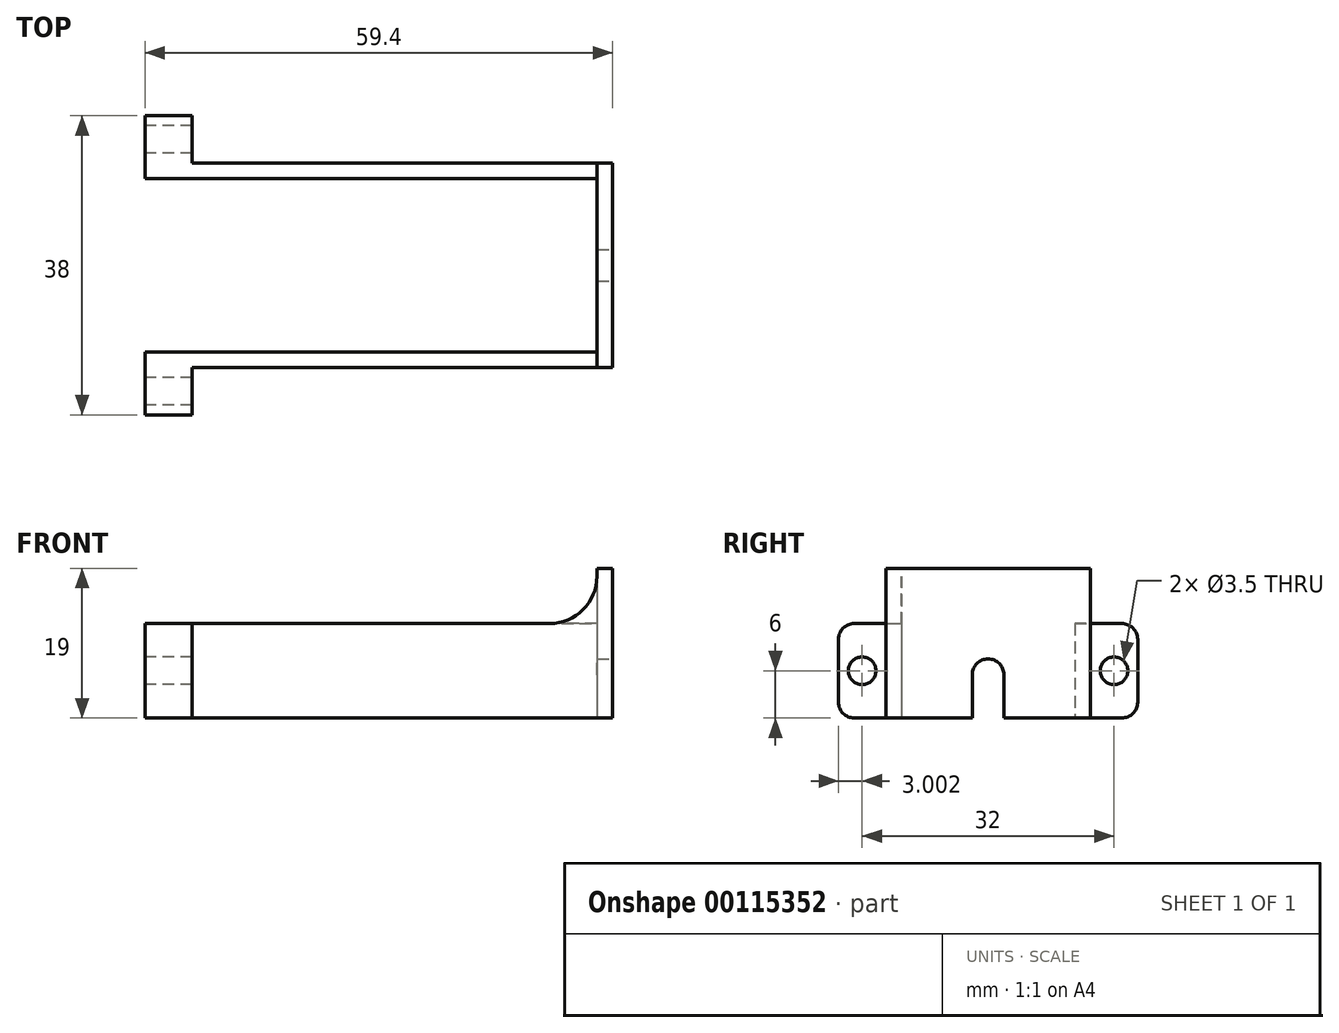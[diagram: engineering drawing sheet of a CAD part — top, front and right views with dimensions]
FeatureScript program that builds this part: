
annotation { "Feature Type Name" : "Feature", "Feature Type Description" : "" }
export const myFeature = defineFeature(function(context is Context, id is Id, definition is map)
    precondition{}
    {
        {
            var Q0;
            Q0=qCreatedBy(makeId("Top.planeOp"),FACE);
            var sketch = newSketch(context, id + "F0", { "sketchPlane" : qUnion([Q0])});
            skLineSegment(sketch, "E0", {"start": v(0, 15.1) * mm, "end": v(0, 7.1) * mm});
            skLineSegment(sketch, "E1", {"start": v(0, 7.1) * mm, "end": v(57.4, 7.1) * mm});
            skLineSegment(sketch, "E2", {"start": v(57.4, 7.1) * mm, "end": v(57.4, -3.9) * mm});
            skLineSegment(sketch, "E3", {"start": v(57.4, -3.9) * mm, "end": v(59.4, -3.9) * mm});
            skLineSegment(sketch, "E4", {"start": v(59.4, -3.9) * mm, "end": v(59.4, 9.1) * mm});
            skLineSegment(sketch, "E5", {"start": v(59.4, 9.1) * mm, "end": v(2, 9.1) * mm});
            skLineSegment(sketch, "E6", {"start": v(2, 9.1) * mm, "end": v(2, 15.1) * mm});
            skLineSegment(sketch, "E7", {"start": v(2, 15.1) * mm, "end": v(0, 15.1) * mm});
            skSolve(sketch);
        }
        {
            var Q0;
            Q0=makeQuery(id+"F0.imprint","IMPRINT",FACE,{"disambiguationData":[TD([[makeQuery(id+"F0.imprint","IMPRINT",EDGE,{"derivedFrom":sQuery(id+"F0.wireOp",EDGE,"E0")}),1.0]])]});
            extrude(context, id + "F1", {"entities" : qUnion([Q0]), "depth" : 12 * mm});
        }
        {
            var Q0;
            Q0=makeQuery(id+"F1.opExtrude","SWEPT_FACE",FACE,{"disambiguationData":[OSD([sQuery(id+"F0.wireOp",EDGE,"E0")])]});
            var sketch = newSketch(context, id + "F2", { "sketchPlane" : qUnion([Q0])});
            skLineSegment(sketch, "E8", {"start": v(-7.1, 6) * mm, "end": v(-12.1, 6) * mm, "construction": true});
            skPoint(sketch, "E8.endSnap0", {"position": v(-7.1, 6) * mm});
            skCircle(sketch, "E9", {"center": v(-12.1, 6) * mm, "radius": 1.75 * mm});
            skSolve(sketch);
        }
        {
            var Q0;
            Q0=makeQuery(id+"F1.opExtrude","SWEPT_FACE",FACE,{"disambiguationData":[OSD([sQuery(id+"F0.wireOp",EDGE,"E6")])]});
            extrude(context, id + "F3", {"entities" : qUnion([Q0]), "operationType" : NewBodyOperationType.ADD, "depth" : 4 * mm});
        }
        {
            var Q0;
            Q0=makeQuery(id+"F2.imprint","IMPRINT",FACE,{"disambiguationData":[TD([[makeQuery(id+"F2.imprint","IMPRINT",EDGE,{"derivedFrom":sQuery(id+"F2.wireOp",EDGE,"E9")}),1.0]])]});
            extrude(context, id + "F4", {"entities" : qUnion([Q0]), "operationType" : NewBodyOperationType.REMOVE, "oppositeDirection" : true, "depth" : 25 * mm});
        }
        {
            var Q0;
            {var subQ0=sQuery(id+"F0.wireOp",EDGE,"E7");var subQ1=sQuery(id+"F0.wireOp",EDGE,"E6");Q0=makeQuery(id+"F3.boolean.opBoolean","MERGE",EDGE,{"derivedFrom":[makeQuery(id+"F1.opExtrude","CAP_EDGE",EDGE,{"disambiguationData":[OSD([subQ0])],"isStart":true}),makeQuery(id+"F3.opExtrude","SWEPT_EDGE",EDGE,{"disambiguationData":[OSD([subQ1,subQ0]),TDD([makeQuery(id+"F1.opExtrude","CAP_VERTEX",VERTEX,{"disambiguationData":[OSD([subQ1,subQ0])],"isStart":true})])]})]});}
            var Q1;
            {var subQ0=sQuery(id+"F0.wireOp",EDGE,"E7");var subQ1=sQuery(id+"F0.wireOp",EDGE,"E6");Q1=makeQuery(id+"F3.boolean.opBoolean","MERGE",EDGE,{"derivedFrom":[makeQuery(id+"F1.opExtrude","CAP_EDGE",EDGE,{"disambiguationData":[OSD([subQ0])],"isStart":false}),makeQuery(id+"F3.opExtrude","SWEPT_EDGE",EDGE,{"disambiguationData":[OSD([subQ1,subQ0]),TDD([makeQuery(id+"F1.opExtrude","CAP_VERTEX",VERTEX,{"disambiguationData":[OSD([subQ1,subQ0])],"isStart":false})])]})]});}
            fillet(context, id + "F5", {"entities" : qUnion([Q0, Q1]), "radius" : 2 * mm, "tangentPropagation" : true, "allowEdgeOverflow" : false});
        }
        {
            var Q0;
            Q0=makeQuery(id+"F1.opExtrude","SWEPT_BODY",BODY,{"disambiguationData":[OSD([sQuery(id+"F0.wireOp",EDGE,"E0"),sQuery(id+"F0.wireOp",EDGE,"E1"),sQuery(id+"F0.wireOp",EDGE,"E2"),sQuery(id+"F0.wireOp",EDGE,"E3"),sQuery(id+"F0.wireOp",EDGE,"E4"),sQuery(id+"F0.wireOp",EDGE,"E5"),sQuery(id+"F0.wireOp",EDGE,"E6"),sQuery(id+"F0.wireOp",EDGE,"E7")])]});
            var Q1;
            Q1=makeQuery(id+"F1.opExtrude","SWEPT_FACE",FACE,{"disambiguationData":[OSD([sQuery(id+"F0.wireOp",EDGE,"E3")])]});
            mirror(context, id + "F6", {"operationType" : NewBodyOperationType.ADD, "entities" : qUnion([Q0]), "mirrorPlane" : qUnion([Q1])});
        }
        {
            var Q0;
            {var subQ0=makeQuery(id+"F1.opExtrude","SWEPT_FACE",FACE,{"disambiguationData":[OSD([sQuery(id+"F0.wireOp",EDGE,"E4")])]});Q0=makeQuery(id+"F6.boolean.opBoolean","MERGE",FACE,{"derivedFrom":[subQ0,makeQuery(id+"F6.opPattern","COPY",FACE,{"derivedFrom":subQ0,"instanceName":"1"})]});}
            var sketch = newSketch(context, id + "F7", { "sketchPlane" : qUnion([Q0])});
            skLineSegment(sketch, "E10", {"start": v(-3.9, 0) * mm, "end": v(-3.9, 7.5) * mm, "construction": true});
            skLineSegment(sketch, "E11", {"start": v(-3.9, 7.5) * mm, "end": v(-5.9, 7.5) * mm});
            skLineSegment(sketch, "E12", {"start": v(-5.9, 7.5) * mm, "end": v(-5.9, 0) * mm});
            skLineSegment(sketch, "E13", {"start": v(-3.9, 7.5) * mm, "end": v(-1.9, 7.5) * mm});
            skLineSegment(sketch, "E14", {"start": v(-1.9, 7.5) * mm, "end": v(-1.9, 0) * mm});
            skSolve(sketch);
        }
        {
            var Q0;
            Q0=makeQuery(id+"F7.imprint","IMPRINT",FACE,{"disambiguationData":[TD([[makeQuery(id+"F7.imprint","IMPRINT",EDGE,{"derivedFrom":sQuery(id+"F7.wireOp",EDGE,"E11")}),1.0]])]});
            extrude(context, id + "F8", {"entities" : qUnion([Q0]), "operationType" : NewBodyOperationType.REMOVE, "oppositeDirection" : true, "depth" : 25 * mm});
        }
        {
            var Q0;
            {var subQ0=sQuery(id+"F0.wireOp",EDGE,"E6");var subQ1=makeQuery(id+"F3.boolean.opBoolean","MERGE",FACE,{"derivedFrom":[makeQuery(id+"F1.opExtrude","CAP_FACE",FACE,{"disambiguationData":[OSD([sQuery(id+"F0.wireOp",EDGE,"E0"),sQuery(id+"F0.wireOp",EDGE,"E1"),sQuery(id+"F0.wireOp",EDGE,"E2"),sQuery(id+"F0.wireOp",EDGE,"E3"),sQuery(id+"F0.wireOp",EDGE,"E4"),sQuery(id+"F0.wireOp",EDGE,"E5"),subQ0,sQuery(id+"F0.wireOp",EDGE,"E7")])],"isStart":false}),makeQuery(id+"F3.opExtrude","SWEPT_FACE",FACE,{"disambiguationData":[OSD([subQ0]),TDD([makeQuery(id+"F1.opExtrude","CAP_EDGE",EDGE,{"disambiguationData":[OSD([subQ0])],"isStart":false})])]})]});Q0=makeQuery(id+"F6.boolean.opBoolean","MERGE",FACE,{"derivedFrom":[subQ1,makeQuery(id+"F6.opPattern","COPY",FACE,{"derivedFrom":subQ1,"instanceName":"1"})]});}
            var sketch = newSketch(context, id + "F9", { "sketchPlane" : qUnion([Q0])});
            skLineSegment(sketch, "E15.bottom", {"start": v(59.4, -16.9) * mm, "end": v(57.4, -16.9) * mm});
            skLineSegment(sketch, "E15.top", {"start": v(59.4, 9.1) * mm, "end": v(57.4, 9.1) * mm});
            skLineSegment(sketch, "E15.left", {"start": v(59.4, -16.9) * mm, "end": v(59.4, 9.1) * mm});
            skLineSegment(sketch, "E15.right", {"start": v(57.4, -16.9) * mm, "end": v(57.4, 9.1) * mm});
            skSolve(sketch);
        }
        {
            var Q0;
            Q0 = qSketchRegion(id + "F9", true);
            extrude(context, id + "F10", {"entities" : qUnion([Q0]), "operationType" : NewBodyOperationType.ADD, "depth" : 7 * mm});
        }
        {
            var Q0;
            {var subQ0=sQuery(id+"F0.wireOp",EDGE,"E1");var subQ7=sQuery(id+"F9.wireOp",EDGE,"E15.right");Q0=makeQuery(id+"F10.boolean.opBoolean","SPLIT",EDGE,{"disambiguationData":[TD([makeQuery(id+"F6.opPattern","COPY",FACE,{"derivedFrom":makeQuery(id+"F1.opExtrude","SWEPT_FACE",FACE,{"disambiguationData":[OSD([subQ0])]}),"instanceName":"1"})])],"derivedFrom":makeQuery(id+"F10.opExtrude","CAP_EDGE",EDGE,{"disambiguationData":[OSD([subQ7])],"isStart":true})});}
            var Q1;
            {var subQ5=sQuery(id+"F0.wireOp",EDGE,"E1");var subQ7=sQuery(id+"F9.wireOp",EDGE,"E15.right");Q1=makeQuery(id+"F10.boolean.opBoolean","SPLIT",EDGE,{"disambiguationData":[TD([makeQuery(id+"F1.opExtrude","SWEPT_FACE",FACE,{"disambiguationData":[OSD([subQ5])]})])],"derivedFrom":makeQuery(id+"F10.opExtrude","CAP_EDGE",EDGE,{"disambiguationData":[OSD([subQ7])],"isStart":true})});}
            fillet(context, id + "F11", {"entities" : qUnion([Q0, Q1]), "radius" : 6 * mm, "tangentPropagation" : true, "allowEdgeOverflow" : false});
        }
        {
            var Q0;
            Q0=makeQuery(id+"F8.boolean.opBoolean","COPY",EDGE,{"derivedFrom":makeQuery(id+"F8.opExtrude","SWEPT_EDGE",EDGE,{"disambiguationData":[OSD([sQuery(id+"F7.wireOp",EDGE,"E13"),sQuery(id+"F7.wireOp",EDGE,"E14")])]})});
            var Q1;
            Q1=makeQuery(id+"F8.boolean.opBoolean","COPY",EDGE,{"derivedFrom":makeQuery(id+"F8.opExtrude","SWEPT_EDGE",EDGE,{"disambiguationData":[OSD([sQuery(id+"F7.wireOp",EDGE,"E11"),sQuery(id+"F7.wireOp",EDGE,"E12")])]})});
            fillet(context, id + "F12", {"entities" : qUnion([Q0, Q1]), "radius" : 2 * mm, "tangentPropagation" : true, "allowEdgeOverflow" : false});
        }
    });
